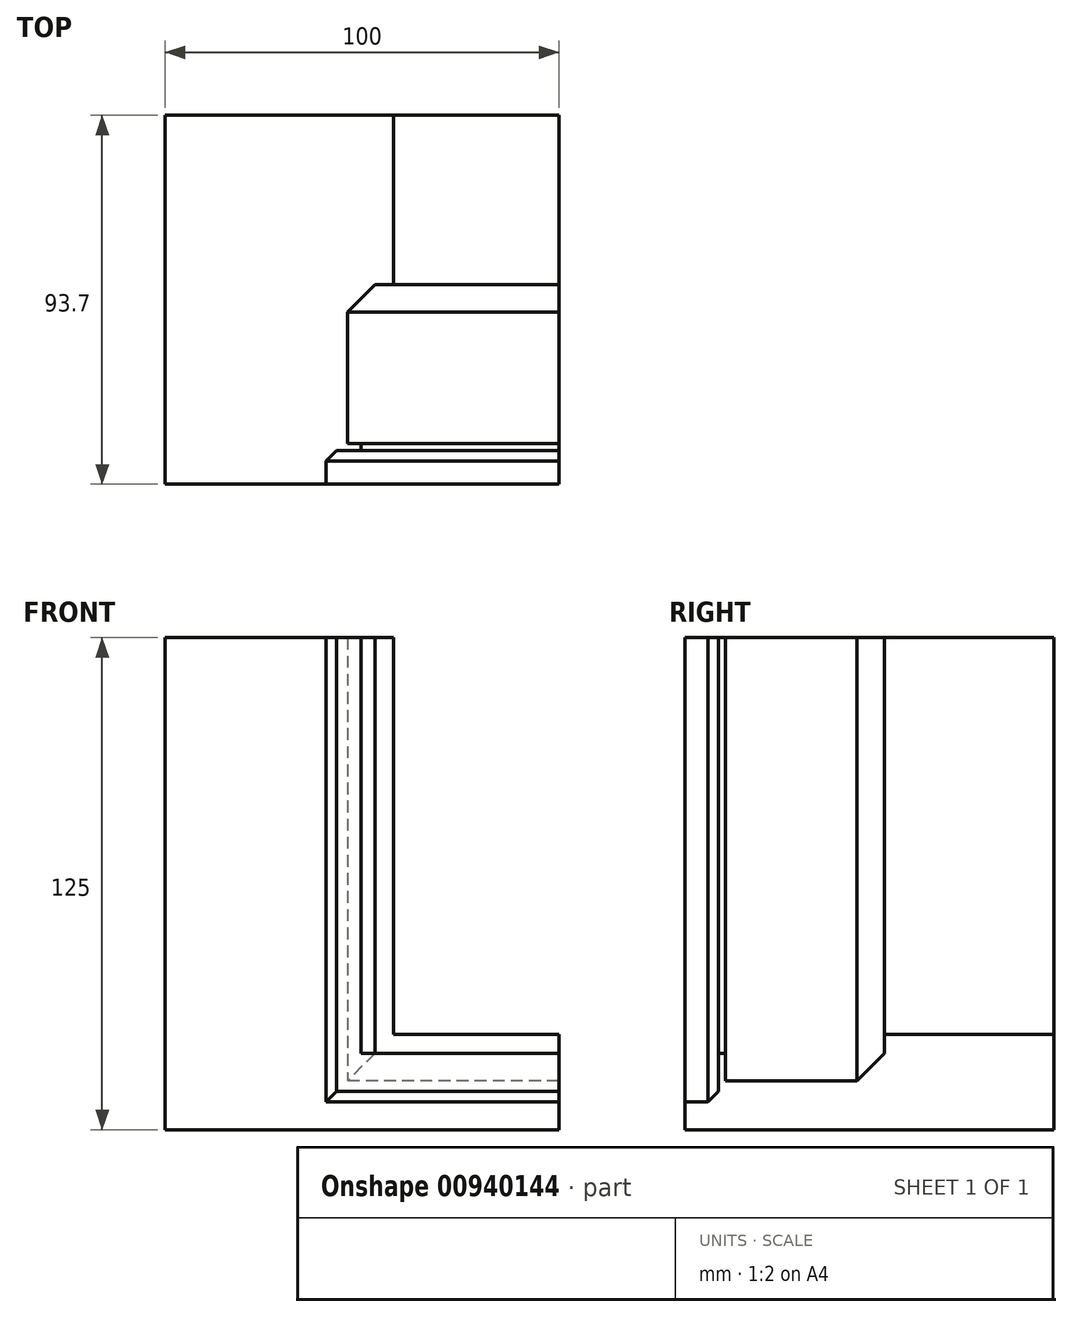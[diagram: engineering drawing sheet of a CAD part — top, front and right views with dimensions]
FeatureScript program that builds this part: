
annotation { "Feature Type Name" : "Feature", "Feature Type Description" : "" }
export const myFeature = defineFeature(function(context is Context, id is Id, definition is map)
    precondition{}
    {
        {
            var Q0;
            Q0=qCreatedBy(makeId("Top.planeOp"),FACE);
            var sketch = newSketch(context, id + "F0", { "sketchPlane" : qUnion([Q0])});
            skLineSegment(sketch, "E0", {"start": v(0, 0) * mm, "end": v(58, 0) * mm});
            skLineSegment(sketch, "E1", {"start": v(58, 0) * mm, "end": v(58, -43) * mm});
            skLineSegment(sketch, "E2", {"start": v(46.3, -50) * mm, "end": v(46.3, -83.4) * mm});
            skLineSegment(sketch, "E3", {"start": v(46.3, -83.4) * mm, "end": v(49.7, -83.4) * mm});
            skLineSegment(sketch, "E4", {"start": v(49.7, -83.4) * mm, "end": v(49.7, -85.2) * mm});
            skLineSegment(sketch, "E5", {"start": v(40.9, -87.8) * mm, "end": v(40.9, -93.7) * mm});
            skLineSegment(sketch, "E6", {"start": v(40.9, -93.7) * mm, "end": v(0, -93.7) * mm});
            skLineSegment(sketch, "E7", {"start": v(0, -93.7) * mm, "end": v(0, 0) * mm});
            skLineSegment(sketch, "E8", {"start": v(58, -43) * mm, "end": v(53.3, -43) * mm});
            skLineSegment(sketch, "E9", {"start": v(46.3, -50) * mm, "end": v(53.3, -43) * mm});
            skLineSegment(sketch, "E10", {"start": v(49.7, -85.2) * mm, "end": v(43.5, -85.2) * mm});
            skLineSegment(sketch, "E11", {"start": v(43.5, -85.2) * mm, "end": v(40.9, -87.8) * mm});
            skSolve(sketch);
        }
        {
            var Q0;
            Q0=makeQuery(id+"F0.imprint","IMPRINT",FACE,{"disambiguationData":[TD([[makeQuery(id+"F0.imprint","IMPRINT",EDGE,{"derivedFrom":sQuery(id+"F0.wireOp",EDGE,"E0")}),-1.0]])]});
            extrude(context, id + "F1", {"entities" : qUnion([Q0]), "depth" : 25 * mm, "offsetDistance" : 25 * mm});
        }
        {
            var Q0;
            Q0=makeQuery(id+"F1.opExtrude","SWEPT_FACE",FACE,{"disambiguationData":[OSD([sQuery(id+"F0.wireOp",EDGE,"E7")])]});
            var sketch = newSketch(context, id + "F2", { "sketchPlane" : qUnion([Q0])});
            skLineSegment(sketch, "E12", {"start": v(0, 0) * mm, "end": v(0, 24.2) * mm});
            skLineSegment(sketch, "E13", {"start": v(0, 24.2) * mm, "end": v(43, 24.2) * mm});
            skLineSegment(sketch, "E14", {"start": v(43, 24.2) * mm, "end": v(43, 19.4) * mm});
            skLineSegment(sketch, "E15", {"start": v(43, 19.4) * mm, "end": v(50, 12.4) * mm});
            skLineSegment(sketch, "E16", {"start": v(50, 12.4) * mm, "end": v(83.4, 12.4) * mm});
            skLineSegment(sketch, "E17", {"start": v(83.4, 12.4) * mm, "end": v(83.4, 19.4) * mm});
            skLineSegment(sketch, "E18", {"start": v(93.7, 7.1) * mm, "end": v(93.7, 0) * mm});
            skLineSegment(sketch, "E19", {"start": v(93.7, 0) * mm, "end": v(0, 0) * mm});
            skLineSegment(sketch, "E20", {"start": v(93.7, 7.1) * mm, "end": v(87.8, 7.1) * mm});
            skLineSegment(sketch, "E21", {"start": v(87.8, 7.1) * mm, "end": v(85.2, 9.7) * mm});
            skLineSegment(sketch, "E22", {"start": v(83.4, 19.4) * mm, "end": v(85.2, 19.4) * mm});
            skLineSegment(sketch, "E23", {"start": v(85.2, 19.4) * mm, "end": v(85.2, 9.7) * mm});
            skSolve(sketch);
        }
        {
            var Q0;
            Q0=makeQuery(id+"F1.opExtrude","CAP_FACE",FACE,{"disambiguationData":[OSD([sQuery(id+"F0.wireOp",EDGE,"E0"),sQuery(id+"F0.wireOp",EDGE,"E1"),sQuery(id+"F0.wireOp",EDGE,"E2"),sQuery(id+"F0.wireOp",EDGE,"E3"),sQuery(id+"F0.wireOp",EDGE,"E4"),sQuery(id+"F0.wireOp",EDGE,"E5"),sQuery(id+"F0.wireOp",EDGE,"E6"),sQuery(id+"F0.wireOp",EDGE,"E7"),sQuery(id+"F0.wireOp",EDGE,"E8"),sQuery(id+"F0.wireOp",EDGE,"E9"),sQuery(id+"F0.wireOp",EDGE,"E10"),sQuery(id+"F0.wireOp",EDGE,"E11")])],"isStart":false});
            extrude(context, id + "F3", {"entities" : qUnion([Q0]), "operationType" : NewBodyOperationType.ADD, "depth" : 100 * mm, "offsetDistance" : 25 * mm});
        }
        {
            var Q0;
            Q0=makeQuery(id+"F2.imprint","IMPRINT",FACE,{"disambiguationData":[TD([[makeQuery(id+"F2.imprint","IMPRINT",EDGE,{"derivedFrom":sQuery(id+"F2.wireOp",EDGE,"E12")}),1.0]])]});
            extrude(context, id + "F4", {"entities" : qUnion([Q0]), "operationType" : NewBodyOperationType.ADD, "oppositeDirection" : true, "depth" : 100 * mm, "offsetDistance" : 25 * mm});
        }
    });
